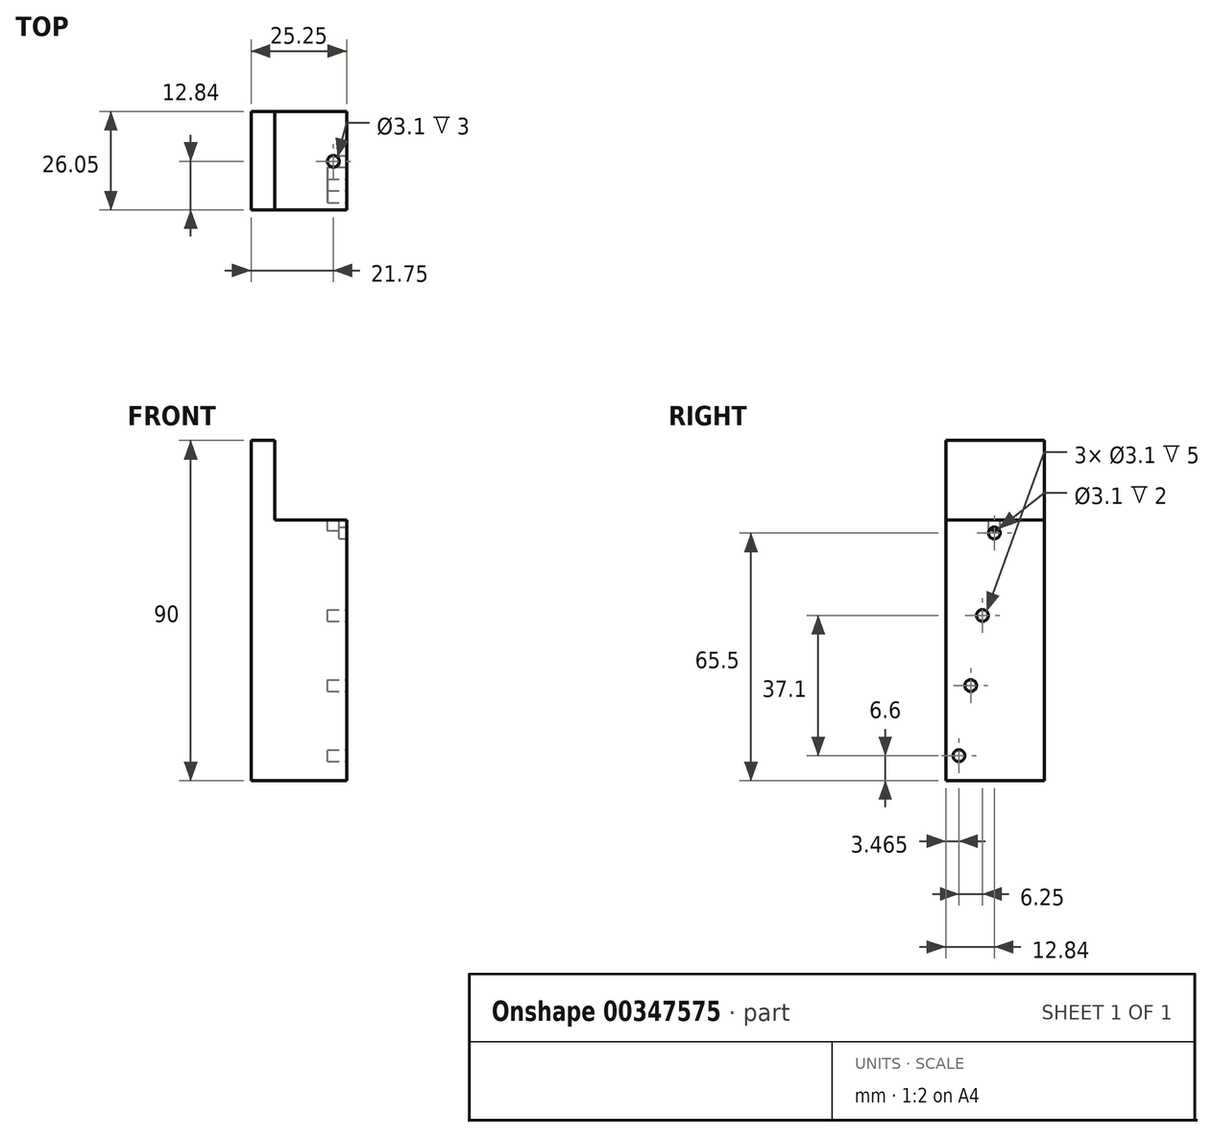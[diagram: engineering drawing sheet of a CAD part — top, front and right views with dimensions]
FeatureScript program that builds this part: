
annotation { "Feature Type Name" : "Feature", "Feature Type Description" : "" }
export const myFeature = defineFeature(function(context is Context, id is Id, definition is map)
    precondition{}
    {
        {
            var Q0;
            Q0=qCreatedBy(makeId("Front.planeOp"),FACE);
            var sketch = newSketch(context, id + "F0", { "sketchPlane" : qUnion([Q0])});
            skLineSegment(sketch, "E0", {"start": v(0, 0) * mm, "end": v(0, 90) * mm});
            skLineSegment(sketch, "E1", {"start": v(0, 90) * mm, "end": v(6.25, 90) * mm});
            skLineSegment(sketch, "E2", {"start": v(6.25, 90) * mm, "end": v(6.25, 69) * mm});
            skLineSegment(sketch, "E3", {"start": v(6.25, 69) * mm, "end": v(25.25, 69) * mm});
            skLineSegment(sketch, "E4", {"start": v(25.25, 69) * mm, "end": v(25.25, 0) * mm});
            skLineSegment(sketch, "E5", {"start": v(25.25, 0) * mm, "end": v(0, 0) * mm});
            skSolve(sketch);
        }
        {
            var Q0;
            Q0=qSketchRegion(id+"F0",true);
            extrude(context, id + "F1", {"entities" : qUnion([Q0]), "oppositeDirection" : true, "depth" : 26.05 * mm});
        }
        {
            var Q0;
            Q0=makeQuery(id+"F1.opExtrude","SWEPT_FACE",FACE,{"disambiguationData":[OSD([sQuery(id+"F0.wireOp",EDGE,"E4")])]});
            var sketch = newSketch(context, id + "F2", { "sketchPlane" : qUnion([Q0])});
            skPoint(sketch, "E6.centerSnap0", {"position": v(13.03, 0) * mm});
            skLineSegment(sketch, "E7", {"start": v(3.47, 6.6) * mm, "end": v(3.47, 25.15) * mm, "construction": true});
            skLineSegment(sketch, "E8", {"start": v(3.47, 25.15) * mm, "end": v(6.6, 25.15) * mm, "construction": true});
            skLineSegment(sketch, "E9", {"start": v(6.6, 25.15) * mm, "end": v(6.6, 43.7) * mm, "construction": true});
            skLineSegment(sketch, "E10", {"start": v(6.6, 43.7) * mm, "end": v(9.72, 43.7) * mm, "construction": true});
            skLineSegment(sketch, "E11", {"start": v(9.72, 43.7) * mm, "end": v(9.72, 65.5) * mm, "construction": true});
            skLineSegment(sketch, "E12", {"start": v(9.72, 65.5) * mm, "end": v(12.84, 65.5) * mm, "construction": true});
            skCircle(sketch, "E13", {"center": v(3.47, 6.6) * mm, "radius": 1.55 * mm});
            skCircle(sketch, "E14", {"center": v(6.6, 25.15) * mm, "radius": 1.55 * mm});
            skCircle(sketch, "E15", {"center": v(9.72, 43.7) * mm, "radius": 1.55 * mm});
            skCircle(sketch, "E16", {"center": v(12.84, 65.5) * mm, "radius": 1.55 * mm});
            skSolve(sketch);
        }
        {
            var Q0;
            Q0=makeQuery(id+"F2.imprint","IMPRINT",FACE,{"disambiguationData":[TD([[makeQuery(id+"F2.imprint","IMPRINT",EDGE,{"derivedFrom":sQuery(id+"F2.wireOp",EDGE,"E15")}),1.0]])]});
            var Q1;
            Q1=makeQuery(id+"F2.imprint","IMPRINT",FACE,{"disambiguationData":[TD([[makeQuery(id+"F2.imprint","IMPRINT",EDGE,{"derivedFrom":sQuery(id+"F2.wireOp",EDGE,"E14")}),1.0]])]});
            var Q2;
            Q2=makeQuery(id+"F2.imprint","IMPRINT",FACE,{"disambiguationData":[TD([[makeQuery(id+"F2.imprint","IMPRINT",EDGE,{"derivedFrom":sQuery(id+"F2.wireOp",EDGE,"E13")}),1.0]])]});
            var Q3;
            Q3=sQuery(id+"F2.wireOp",EDGE,"E16");
            var Q4;
            Q4=sQuery(id+"F2.wireOp",EDGE,"E15");
            var Q5;
            Q5=sQuery(id+"F2.wireOp",EDGE,"E14");
            var Q6;
            Q6=sQuery(id+"F2.wireOp",EDGE,"E13");
            extrude(context, id + "F3", {"entities" : qUnion([Q0, Q1, Q2]), "operationType" : NewBodyOperationType.REMOVE, "surfaceEntities" : qUnion([Q3, Q4, Q5, Q6]), "oppositeDirection" : true, "depth" : 5 * mm});
        }
        {
            var Q0;
            Q0=makeQuery(id+"F1.opExtrude","SWEPT_FACE",FACE,{"disambiguationData":[OSD([sQuery(id+"F0.wireOp",EDGE,"E3")])]});
            var sketch = newSketch(context, id + "F4", { "sketchPlane" : qUnion([Q0])});
            skCircle(sketch, "E17", {"center": v(21.75, 12.84) * mm, "radius": 1.55 * mm});
            skSolve(sketch);
        }
        {
            var Q0;
            Q0=makeQuery(id+"F4.imprint","IMPRINT",FACE,{"disambiguationData":[TD([[makeQuery(id+"F4.imprint","IMPRINT",EDGE,{"derivedFrom":sQuery(id+"F4.wireOp",EDGE,"E17")}),1.0]])]});
            var Q1;
            Q1=sQuery(id+"F4.wireOp",EDGE,"E17");
            extrude(context, id + "F5", {"entities" : qUnion([Q0]), "operationType" : NewBodyOperationType.REMOVE, "surfaceEntities" : qUnion([Q1]), "oppositeDirection" : true, "depth" : 3 * mm});
        }
        {
            var Q0;
            Q0=makeQuery(id+"F2.imprint","IMPRINT",FACE,{"disambiguationData":[TD([[makeQuery(id+"F2.imprint","IMPRINT",EDGE,{"derivedFrom":sQuery(id+"F2.wireOp",EDGE,"E16")}),1.0]])]});
            extrude(context, id + "F6", {"entities" : qUnion([Q0]), "operationType" : NewBodyOperationType.REMOVE, "oppositeDirection" : true, "depth" : 2 * mm});
        }
    });
